FCSTD DOCUMENT  (FreeCAD 0.16R6698 (Git))
Label: xy-motor-mount
License: All rights reserved
LicenseURL: http://de.wikipedia.org/wiki/Alle_Rechte_vorbehalten
objects: Sketcher::SketchObject×1
note: 1 computed .brp shape members not serialized (recipe doc carries the construction recipe); baked Part::Feature solids carry a one-line shape summary decoded from their .brp

FEATURE [Sketcher::SketchObject] Sketch
  sketch-geometry (14):
    g0: LineSegment StartX=10 StartY=-89.2684 StartZ=0 EndX=-51.7708 EndY=-27.4975 EndZ=0
    g1: LineSegment StartX=-51.7708 StartY=-27.4975 StartZ=0 EndX=-51.7708 EndY=-23.4975 EndZ=0
    g2: LineSegment StartX=-51.7708 StartY=-23.4975 StartZ=0 EndX=-14 EndY=-23.4975 EndZ=0
    g3: LineSegment StartX=-14 StartY=-23.4975 StartZ=0 EndX=-14 EndY=18.9654 EndZ=0
    g4: LineSegment StartX=-14 StartY=18.9654 StartZ=0 EndX=-57.7202 EndY=18.9654 EndZ=0
    g5: LineSegment StartX=-57.7202 StartY=18.9654 StartZ=0 EndX=-57.7202 EndY=22.9654 EndZ=0
    g6: LineSegment StartX=-57.7202 StartY=22.9654 StartZ=0 EndX=-10 EndY=22.9654 EndZ=0
    g7: LineSegment StartX=-10 StartY=22.9654 StartZ=0 EndX=-10 EndY=0 EndZ=0
    g8: LineSegment StartX=-10 StartY=0 StartZ=0 EndX=10 EndY=0 EndZ=0
    g9: LineSegment StartX=10 StartY=0 StartZ=0 EndX=10 EndY=-89.2684 EndZ=0
    g10: Circle CenterX=0 CenterY=-15 CenterZ=0 NormalX=0 NormalY=0 NormalZ=1 Radius=3.08446
    g11: Circle CenterX=0 CenterY=-30 CenterZ=0 NormalX=0 NormalY=0 NormalZ=1 Radius=3.08446
    g12: Circle CenterX=0 CenterY=-45 CenterZ=0 NormalX=0 NormalY=0 NormalZ=1 Radius=3.08446
    g13: Circle CenterX=0 CenterY=-60 CenterZ=0 NormalX=0 NormalY=0 NormalZ=1 Radius=3.08446
  constraints (37):
    c: Coincident(g0,g1)
    c: Coincident(g1,g2)
    c: Horizontal(g2)
    c: Coincident(g2,g3)
    c: Vertical(g3)
    c: Coincident(g3,g4)
    c: Horizontal(g4)
    c: Coincident(g4,g5)
    c: Coincident(g5,g6)
    c: Horizontal(g6)
    c: Coincident(g6,g7)
    c: PointOnObject(g7,g-1)
    c: Vertical(g7)
    c: Coincident(g7,g8)
    c: Horizontal(g8)
    c: Coincident(g8,g9)
    c: Coincident(g9,g0)
    c: Vertical(g9)
    c: Vertical(g1)
    c: DistanceY(g1,g1) = 4
    c: Vertical(g5)
    c: DistanceY(g4,g5) = 4
    c: Angle(g9,g0) = 0.785398
    c: DistanceX(g3,g6) = 4
    c: DistanceX(g7,g8) = 20
    c: Symmetric(g7,g8,g-2)
    c: PointOnObject(g10,g-2)
    c: PointOnObject(g11,g-2)
    c: PointOnObject(g12,g-2)
    c: PointOnObject(g13,g-2)
    c: Equal(g13,g12)
    c: Equal(g12,g11)
    c: Equal(g11,g10)
    c: DistanceY(g10,g-1) = 15
    c: DistanceY(g11,g10) = 15
    c: DistanceY(g12,g11) = 15
    c: DistanceY(g13,g12) = 15
